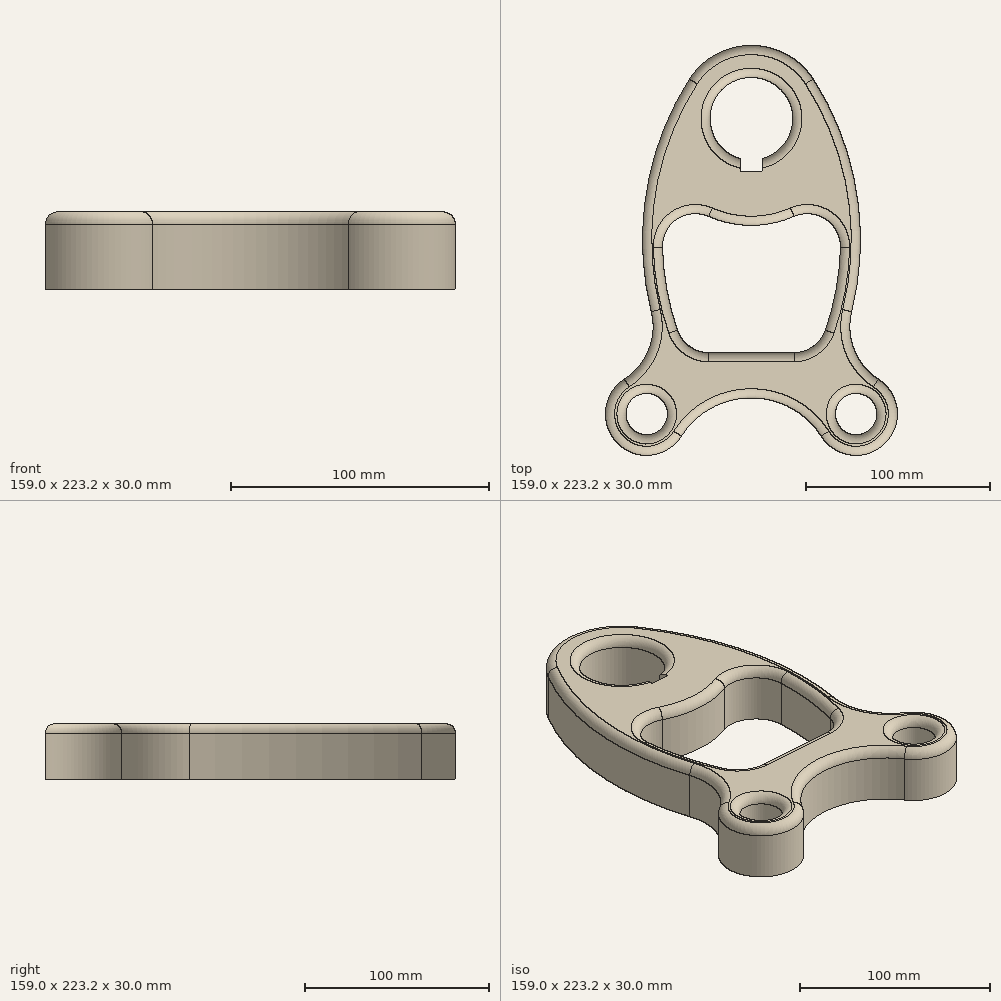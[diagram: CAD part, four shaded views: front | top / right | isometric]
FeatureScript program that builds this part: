
annotation { "Feature Type Name" : "Feature", "Feature Type Description" : "" }
export const myFeature = defineFeature(function(context is Context, id is Id, definition is map)
    precondition{}
    {
        {
            var Q0;
            Q0=qCreatedBy(makeId("Top.planeOp"),FACE);
            var sketch = newSketch(context, id + "F0", { "sketchPlane" : qUnion([Q0])});
            skPoint(sketch, "E0", {"position": v(0, -45.36) * mm});
            skCircle(sketch, "E1", {"center": v(-57, -39.83) * mm, "radius": 11.25 * mm});
            skCircle(sketch, "E2", {"center": v(-57, -39.83) * mm, "radius": 22.5 * mm});
            skCircle(sketch, "E3", {"center": v(57, -39.83) * mm, "radius": 11.25 * mm});
            skCircle(sketch, "E4", {"center": v(57, -39.83) * mm, "radius": 22.5 * mm});
            skLineSegment(sketch, "E5", {"start": v(-57.91, -6.31) * mm, "end": v(-56.57, -6.31) * mm});
            skArc(sketch, "E6", {"start": v(38, -51.89) * mm, "mid": v(0, -30.99) * mm, "end": v(-38, -51.89) * mm});
            skArc(sketch, "E7", {"start": v(-69.17, -20.9) * mm, "mid": v(-55.95, -4.85) * mm, "end": v(-54.55, 15.9) * mm});
            skPoint(sketch, "E8.endSnap0", {"position": v(0, -30.99) * mm});
            skCircle(sketch, "E9", {"center": v(0, 120.89) * mm, "radius": 40 * mm});
            skLineSegment(sketch, "E10", {"start": v(-5.75, 92.39) * mm, "end": v(-5.75, 99.14) * mm});
            skLineSegment(sketch, "E11", {"start": v(-5.75, 92.39) * mm, "end": v(5.75, 92.39) * mm});
            skLineSegment(sketch, "E12", {"start": v(5.75, 92.39) * mm, "end": v(5.75, 99.14) * mm});
            skArc(sketch, "E13", {"start": v(5.75, 99.14) * mm, "mid": v(0, 143.39) * mm, "end": v(-5.75, 99.14) * mm});
            skArc(sketch, "E14", {"start": v(-33.66, 142.5) * mm, "mid": v(-57.17, 81.35) * mm, "end": v(-54.55, 15.9) * mm});
            skArc(sketch, "E15.MirrorCS", {"start": v(33.66, 142.5) * mm, "mid": v(57.17, 81.35) * mm, "end": v(54.55, 15.9) * mm});
            skArc(sketch, "E16.MirrorCS", {"start": v(69.17, -20.9) * mm, "mid": v(55.95, -4.85) * mm, "end": v(54.55, 15.9) * mm});
            skPoint(sketch, "E17", {"position": v(-102.7, 63.89) * mm});
            skArc(sketch, "E18", {"start": v(-23.23, 67.75) * mm, "mid": v(0, 62.89) * mm, "end": v(23.23, 67.75) * mm});
            skArc(sketch, "E19", {"start": v(-48.44, 50.75) * mm, "mid": v(-46.07, 27.98) * mm, "end": v(-40.3, 5.84) * mm});
            skLineSegment(sketch, "E20", {"start": v(56.24, -6.31) * mm, "end": v(57.76, -8.7) * mm});
            skLineSegment(sketch, "E21.trimOffspring", {"start": v(-23.27, -6.31) * mm, "end": v(23.27, -6.31) * mm});
            skArc(sketch, "E22.MirrorCS", {"start": v(48.44, 50.75) * mm, "mid": v(46.07, 27.98) * mm, "end": v(40.3, 5.84) * mm});
            skArc(sketch, "E23", {"start": v(-23.23, 67.75) * mm, "mid": v(-40.5, 66.18) * mm, "end": v(-48.44, 50.75) * mm});
            skArc(sketch, "E24.MirrorC", {"start": v(23.23, 67.75) * mm, "mid": v(40.5, 66.18) * mm, "end": v(48.44, 50.75) * mm});
            skArc(sketch, "E25", {"start": v(-40.3, 5.84) * mm, "mid": v(-33.73, -2.97) * mm, "end": v(-23.27, -6.31) * mm});
            skArc(sketch, "E26.MirrorC", {"start": v(40.3, 5.84) * mm, "mid": v(33.73, -2.97) * mm, "end": v(23.27, -6.31) * mm});
            skPoint(sketch, "E27.end.orphan", {"position": v(-102.7, 120.89) * mm});
            skPoint(sketch, "E28.orphan", {"position": v(-45.5, 84.92) * mm});
            skPoint(sketch, "E29.orphan", {"position": v(45.5, 84.92) * mm});
            skPoint(sketch, "E30.orphan", {"position": v(-35.52, -6.31) * mm});
            skPoint(sketch, "E31.orphan", {"position": v(35.52, -6.31) * mm});
            skSolve(sketch);
        }
        {
            var Q0;
            Q0=makeQuery(id+"F0.imprint","IMPRINT",FACE,{"disambiguationData":[TD([[makeQuery(id+"F0.imprint","IMPRINT",EDGE,{"derivedFrom":sQuery(id+"F0.wireOp",EDGE,"E10")}),1.0]])]});
            var Q1;
            {var subQ5=sQuery(id+"F0.wireOp",EDGE,"E6");Q1=makeQuery(id+"F0.imprint","IMPRINT",FACE,{"disambiguationData":[TD([[makeQuery(id+"F0.imprint","IMPRINT",EDGE,{"derivedFrom":subQ5}),-1.0]])]});}
            var Q2;
            Q2=makeQuery(id+"F0.imprint","IMPRINT",FACE,{"disambiguationData":[TD([[makeQuery(id+"F0.imprint","IMPRINT",EDGE,{"derivedFrom":sQuery(id+"F0.wireOp",EDGE,"E1")}),-1.0]])]});
            var Q3;
            Q3=makeQuery(id+"F0.imprint","IMPRINT",FACE,{"disambiguationData":[TD([[makeQuery(id+"F0.imprint","IMPRINT",EDGE,{"derivedFrom":sQuery(id+"F0.wireOp",EDGE,"E3")}),-1.0]])]});
            extrude(context, id + "F1", {"entities" : qUnion([Q0, Q1, Q2, Q3]), "depth" : 30 * mm});
        }
        {
            var Q0;
            Q0=makeQuery(id+"F1.opExtrude","CAP_EDGE",EDGE,{"disambiguationData":[OSD([sQuery(id+"F0.wireOp",EDGE,"E13")])],"isStart":false});
            var Q1;
            Q1=makeQuery(id+"F1.opExtrude","CAP_EDGE",EDGE,{"disambiguationData":[OSD([sQuery(id+"F0.wireOp",EDGE,"E9")])],"isStart":false});
            var Q2;
            Q2=makeQuery(id+"F1.opExtrude","CAP_EDGE",EDGE,{"disambiguationData":[OSD([sQuery(id+"F0.wireOp",EDGE,"E14")])],"isStart":false});
            var Q3;
            Q3=makeQuery(id+"F1.opExtrude","CAP_EDGE",EDGE,{"disambiguationData":[OSD([sQuery(id+"F0.wireOp",EDGE,"E7")])],"isStart":false});
            var Q4;
            Q4=makeQuery(id+"F1.opExtrude","CAP_EDGE",EDGE,{"disambiguationData":[OSD([sQuery(id+"F0.wireOp",EDGE,"E2")])],"isStart":false});
            var Q5;
            Q5=makeQuery(id+"F1.opExtrude","CAP_EDGE",EDGE,{"disambiguationData":[OSD([sQuery(id+"F0.wireOp",EDGE,"E6")])],"isStart":false});
            var Q6;
            Q6=makeQuery(id+"F1.opExtrude","CAP_EDGE",EDGE,{"disambiguationData":[OSD([sQuery(id+"F0.wireOp",EDGE,"E4")])],"isStart":false});
            var Q7;
            Q7=makeQuery(id+"F1.opExtrude","CAP_EDGE",EDGE,{"disambiguationData":[OSD([sQuery(id+"F0.wireOp",EDGE,"E16.MirrorCS")])],"isStart":false});
            var Q8;
            Q8=makeQuery(id+"F1.opExtrude","CAP_EDGE",EDGE,{"disambiguationData":[OSD([sQuery(id+"F0.wireOp",EDGE,"E15.MirrorCS")])],"isStart":false});
            var Q9;
            Q9=makeQuery(id+"F1.opExtrude","CAP_EDGE",EDGE,{"disambiguationData":[OSD([sQuery(id+"F0.wireOp",EDGE,"E18")])],"isStart":false});
            var Q10;
            Q10=makeQuery(id+"F1.opExtrude","CAP_EDGE",EDGE,{"disambiguationData":[OSD([sQuery(id+"F0.wireOp",EDGE,"E24.MirrorC")])],"isStart":false});
            var Q11;
            Q11=makeQuery(id+"F1.opExtrude","CAP_EDGE",EDGE,{"disambiguationData":[OSD([sQuery(id+"F0.wireOp",EDGE,"E22.MirrorCS")])],"isStart":false});
            var Q12;
            Q12=makeQuery(id+"F1.opExtrude","CAP_EDGE",EDGE,{"disambiguationData":[OSD([sQuery(id+"F0.wireOp",EDGE,"E26.MirrorC")])],"isStart":false});
            var Q13;
            Q13=makeQuery(id+"F1.opExtrude","CAP_EDGE",EDGE,{"disambiguationData":[OSD([sQuery(id+"F0.wireOp",EDGE,"E21.trimOffspring")])],"isStart":false});
            var Q14;
            Q14=makeQuery(id+"F1.opExtrude","CAP_EDGE",EDGE,{"disambiguationData":[OSD([sQuery(id+"F0.wireOp",EDGE,"E25")])],"isStart":false});
            var Q15;
            Q15=makeQuery(id+"F1.opExtrude","CAP_EDGE",EDGE,{"disambiguationData":[OSD([sQuery(id+"F0.wireOp",EDGE,"E19")])],"isStart":false});
            var Q16;
            Q16=makeQuery(id+"F1.opExtrude","CAP_EDGE",EDGE,{"disambiguationData":[OSD([sQuery(id+"F0.wireOp",EDGE,"E23")])],"isStart":false});
            var Q17;
            Q17=makeQuery(id+"F1.opExtrude","CAP_EDGE",EDGE,{"disambiguationData":[OSD([sQuery(id+"F0.wireOp",EDGE,"E3")])],"isStart":false});
            var Q18;
            Q18=makeQuery(id+"F1.opExtrude","CAP_EDGE",EDGE,{"disambiguationData":[OSD([sQuery(id+"F0.wireOp",EDGE,"E1")])],"isStart":false});
            fillet(context, id + "F2", {"entities" : qUnion([Q0, Q1, Q2, Q3, Q4, Q5, Q6, Q7, Q8, Q9, Q10, Q11, Q12, Q13, Q14, Q15, Q16, Q17, Q18]), "radius" : 5 * mm, "tangentPropagation" : true, "allowEdgeOverflow" : false});
        }
    });
